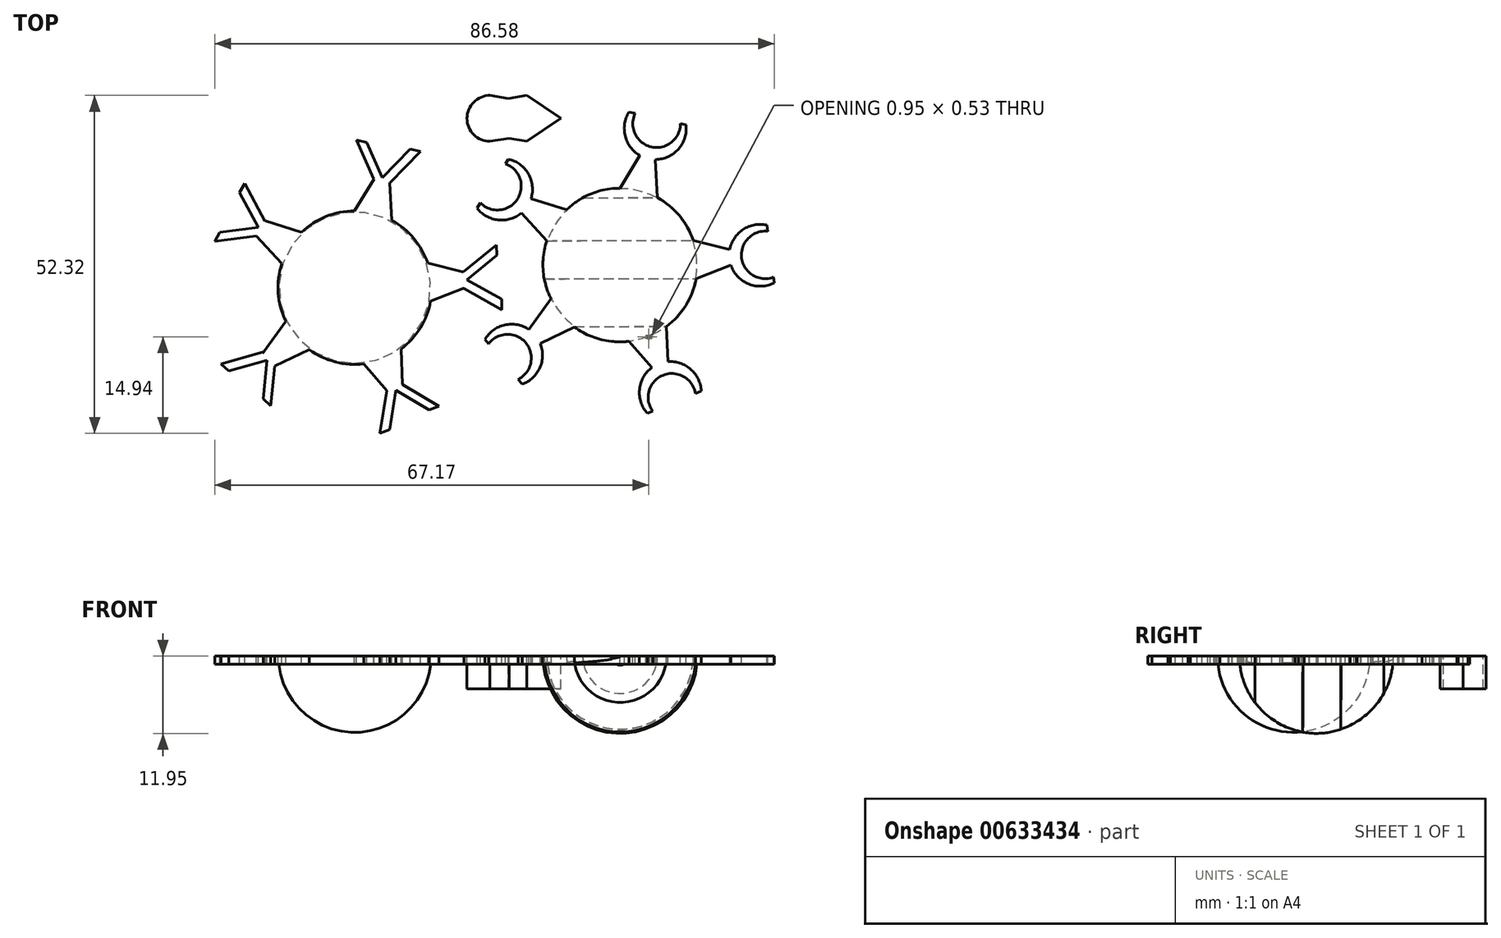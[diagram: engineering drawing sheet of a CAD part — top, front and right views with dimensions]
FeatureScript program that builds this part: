
annotation { "Feature Type Name" : "Feature", "Feature Type Description" : "" }
export const myFeature = defineFeature(function(context is Context, id is Id, definition is map)
    precondition{}
    {
        {
            var Q0;
            Q0=qCreatedBy(makeId("Top.planeOp"),FACE);
            var sketch = newSketch(context, id + "F0", { "sketchPlane" : qUnion([Q0])});
            skCircle(sketch, "E0.cCircle", {"center": v(0, 3.73) * mm, "radius": 12.26 * mm, "construction": true});
            skLineSegment(sketch, "E0.3", {"start": v(4.56, -7.66) * mm, "end": v(3.93, -7.5) * mm});
            skLineSegment(sketch, "E1", {"start": v(4.56, -7.66) * mm, "end": v(4.42, -7.3) * mm});
            skLineSegment(sketch, "E2", {"start": v(-14.6, 12.91) * mm, "end": v(-13.88, 14.05) * mm});
            skLineSegment(sketch, "E3", {"start": v(-13.88, 14.05) * mm, "end": v(-8.26, 12.28) * mm});
            skLineSegment(sketch, "E4", {"start": v(-14.6, 12.91) * mm, "end": v(-15.32, 11.77) * mm});
            skLineSegment(sketch, "E5", {"start": v(-15.32, 11.77) * mm, "end": v(-11.3, 7.45) * mm});
            skPoint(sketch, "E6.start.orphan", {"position": v(-10.38, 10.26) * mm});
            skLineSegment(sketch, "E7", {"start": v(-13.28, -7.35) * mm, "end": v(-14.16, -6.3) * mm});
            skLineSegment(sketch, "E8", {"start": v(-14.16, -6.3) * mm, "end": v(-10.69, -1.48) * mm});
            skLineSegment(sketch, "E9", {"start": v(-13.28, -7.35) * mm, "end": v(-12.38, -8.43) * mm});
            skLineSegment(sketch, "E10", {"start": v(-12.38, -8.43) * mm, "end": v(-7.05, -5.85) * mm});
            skLineSegment(sketch, "E11", {"start": v(6.18, -11.7) * mm, "end": v(4.96, -12.2) * mm});
            skLineSegment(sketch, "E12", {"start": v(4.96, -12.2) * mm, "end": v(1.38, -8.08) * mm});
            skLineSegment(sketch, "E13", {"start": v(6.18, -11.7) * mm, "end": v(7.36, -11.23) * mm});
            skLineSegment(sketch, "E14", {"start": v(7.36, -11.23) * mm, "end": v(7.16, -5.77) * mm});
            skLineSegment(sketch, "E15", {"start": v(17.02, 4.87) * mm, "end": v(17.1, 3.73) * mm});
            skLineSegment(sketch, "E16", {"start": v(17.1, 3.73) * mm, "end": v(11.7, 1.62) * mm});
            skLineSegment(sketch, "E17", {"start": v(17.02, 4.87) * mm, "end": v(16.94, 6.1) * mm});
            skLineSegment(sketch, "E18", {"start": v(16.94, 6.1) * mm, "end": v(11.26, 7.53) * mm});
            skLineSegment(sketch, "E19", {"start": v(5.42, 20.04) * mm, "end": v(5.72, 14.15) * mm});
            skLineSegment(sketch, "E20", {"start": v(3, 20.65) * mm, "end": v(-0.04, 15.62) * mm});
            skArc(sketch, "E21", {"start": v(-7.05, -5.85) * mm, "mid": v(-3.05, -7.76) * mm, "end": v(1.38, -8.08) * mm});
            skPoint(sketch, "E22.orphan", {"position": v(0, -6.5) * mm});
            skArc(sketch, "E23.trimOffspring", {"start": v(-11.3, 7.45) * mm, "mid": v(-11.86, 2.92) * mm, "end": v(-10.69, -1.48) * mm});
            skArc(sketch, "E24.trimOffspring", {"start": v(-0.04, 15.62) * mm, "mid": v(-4.47, 14.74) * mm, "end": v(-8.26, 12.28) * mm});
            skPoint(sketch, "E0.1.start.orphan", {"position": v(3, 15.62) * mm});
            skArc(sketch, "E25.trimOffspring", {"start": v(11.26, 7.53) * mm, "mid": v(9.12, 11.36) * mm, "end": v(5.72, 14.15) * mm});
            skLineSegment(sketch, "E26.trimOffspring", {"start": v(4.9, -7.1) * mm, "end": v(4.56, -7.66) * mm});
            skArc(sketch, "E27.trimOffspring", {"start": v(7.16, -5.77) * mm, "mid": v(10.13, -2.5) * mm, "end": v(11.7, 1.62) * mm});
            skArc(sketch, "E28", {"start": v(2.3, 27.2) * mm, "mid": v(4.82, 22) * mm, "end": v(9.3, 25.64) * mm});
            skArc(sketch, "E29", {"start": v(1.36, 27.41) * mm, "mid": v(0.75, 23.72) * mm, "end": v(2.98, 20.72) * mm});
            skLineSegment(sketch, "E30", {"start": v(1.36, 27.41) * mm, "end": v(2.3, 27.2) * mm});
            skLineSegment(sketch, "E31.trimOffspring", {"start": v(9.3, 25.64) * mm, "end": v(10.15, 25.45) * mm});
            skArc(sketch, "E32.trimOffspring", {"start": v(5.45, 20.06) * mm, "mid": v(9.01, 21.7) * mm, "end": v(10.15, 25.45) * mm});
            skLineSegment(sketch, "E33", {"start": v(3, 20.65) * mm, "end": v(2.98, 20.72) * mm});
            skPoint(sketch, "E34.orphan", {"position": v(4.2, 20.35) * mm});
            skLineSegment(sketch, "E35", {"start": v(5.42, 20.04) * mm, "end": v(5.45, 20.06) * mm});
            skArc(sketch, "E36", {"start": v(-21.63, 13.35) * mm, "mid": v(-15.9, 13.93) * mm, "end": v(-17.78, 19.38) * mm});
            skArc(sketch, "E37", {"start": v(-22.16, 12.53) * mm, "mid": v(-18.9, 10.7) * mm, "end": v(-15.32, 11.77) * mm});
            skLineSegment(sketch, "E38", {"start": v(-22.16, 12.53) * mm, "end": v(-21.63, 13.35) * mm});
            skLineSegment(sketch, "E39.trimOffspring", {"start": v(-17.78, 19.38) * mm, "end": v(-17.3, 20.12) * mm});
            skArc(sketch, "E40.trimOffspring", {"start": v(-13.85, 13.86) * mm, "mid": v(-14.17, 17.77) * mm, "end": v(-17.3, 20.12) * mm});
            skArc(sketch, "E41", {"start": v(22.8, 8.95) * mm, "mid": v(18.77, 4.81) * mm, "end": v(23.72, 1.84) * mm});
            skArc(sketch, "E42", {"start": v(22.67, 9.9) * mm, "mid": v(19, 9.22) * mm, "end": v(16.94, 6.1) * mm});
            skLineSegment(sketch, "E43", {"start": v(22.67, 9.9) * mm, "end": v(22.8, 8.95) * mm});
            skLineSegment(sketch, "E44.trimOffspring", {"start": v(23.72, 1.84) * mm, "end": v(23.83, 0.97) * mm});
            skArc(sketch, "E45.trimOffspring", {"start": v(17.16, 3.55) * mm, "mid": v(19.92, 0.77) * mm, "end": v(23.83, 0.97) * mm});
            skLineSegment(sketch, "E46", {"start": v(17.16, 3.55) * mm, "end": v(17.1, 3.73) * mm});
            skArc(sketch, "E47", {"start": v(-15.8, -13.97) * mm, "mid": v(-14.62, -8.33) * mm, "end": v(-20.38, -8.47) * mm});
            skArc(sketch, "E48", {"start": v(-15.17, -14.72) * mm, "mid": v(-12.44, -12.17) * mm, "end": v(-12.38, -8.43) * mm});
            skLineSegment(sketch, "E49", {"start": v(-15.17, -14.72) * mm, "end": v(-15.8, -13.97) * mm});
            skLineSegment(sketch, "E50.trimOffspring", {"start": v(-20.38, -8.47) * mm, "end": v(-20.94, -7.8) * mm});
            skArc(sketch, "E51.trimOffspring", {"start": v(-13.93, -6.4) * mm, "mid": v(-17.75, -5.53) * mm, "end": v(-20.94, -7.8) * mm});
            skArc(sketch, "E52", {"start": v(11.62, -16.16) * mm, "mid": v(6.59, -13.34) * mm, "end": v(5, -18.89) * mm});
            skArc(sketch, "E53", {"start": v(12.52, -15.79) * mm, "mid": v(10.9, -12.42) * mm, "end": v(7.36, -11.23) * mm});
            skLineSegment(sketch, "E54", {"start": v(12.52, -15.79) * mm, "end": v(11.62, -16.16) * mm});
            skLineSegment(sketch, "E55.trimOffspring", {"start": v(5, -18.89) * mm, "end": v(4.19, -19.22) * mm});
            skArc(sketch, "E56.trimOffspring", {"start": v(4.95, -12.11) * mm, "mid": v(2.98, -15.5) * mm, "end": v(4.19, -19.22) * mm});
            skArc(sketch, "E57", {"start": v(0, -8.16) * mm, "mid": v(11.92, 3.75) * mm, "end": v(-0.04, 15.62) * mm});
            skLineSegment(sketch, "E58", {"start": v(0, -8.16) * mm, "end": v(-0.04, 15.62) * mm});
            skSolve(sketch);
        }
        {
            var Q0;
            Q0=qCreatedBy(makeId("Top.planeOp"),FACE);
            var sketch = newSketch(context, id + "F1", { "sketchPlane" : qUnion([Q0])});
            skCircle(sketch, "E59.cCircle", {"center": v(-41.06, 0.22) * mm, "radius": 12.26 * mm, "construction": true});
            skLineSegment(sketch, "E60", {"start": v(-55.66, 9.4) * mm, "end": v(-54.94, 10.54) * mm});
            skLineSegment(sketch, "E61", {"start": v(-54.94, 10.54) * mm, "end": v(-49.32, 8.78) * mm});
            skLineSegment(sketch, "E62", {"start": v(-55.66, 9.4) * mm, "end": v(-56.38, 8.26) * mm});
            skLineSegment(sketch, "E63", {"start": v(-56.38, 8.26) * mm, "end": v(-52.35, 3.94) * mm});
            skPoint(sketch, "E64.start.orphan", {"position": v(-51.44, 6.75) * mm});
            skLineSegment(sketch, "E65", {"start": v(-54.34, -10.85) * mm, "end": v(-55.22, -9.8) * mm});
            skLineSegment(sketch, "E66", {"start": v(-55.22, -9.8) * mm, "end": v(-51.75, -4.98) * mm});
            skLineSegment(sketch, "E67", {"start": v(-54.34, -10.85) * mm, "end": v(-53.44, -11.94) * mm});
            skLineSegment(sketch, "E68", {"start": v(-53.44, -11.94) * mm, "end": v(-48.11, -9.35) * mm});
            skLineSegment(sketch, "E69", {"start": v(-34.88, -15.21) * mm, "end": v(-36.1, -15.7) * mm});
            skLineSegment(sketch, "E70", {"start": v(-36.1, -15.7) * mm, "end": v(-39.68, -11.59) * mm});
            skLineSegment(sketch, "E71", {"start": v(-34.88, -15.21) * mm, "end": v(-33.7, -14.74) * mm});
            skLineSegment(sketch, "E72", {"start": v(-33.7, -14.74) * mm, "end": v(-33.9, -9.27) * mm});
            skLineSegment(sketch, "E73", {"start": v(-24.04, 1.36) * mm, "end": v(-23.96, 0.22) * mm});
            skLineSegment(sketch, "E74", {"start": v(-23.96, 0.22) * mm, "end": v(-29.36, -1.88) * mm});
            skLineSegment(sketch, "E75", {"start": v(-24.04, 1.36) * mm, "end": v(-24.12, 2.6) * mm});
            skLineSegment(sketch, "E76", {"start": v(-24.12, 2.6) * mm, "end": v(-29.8, 4.03) * mm});
            skLineSegment(sketch, "E77", {"start": v(-36.86, 16.85) * mm, "end": v(-35.64, 16.54) * mm});
            skLineSegment(sketch, "E78", {"start": v(-35.64, 16.54) * mm, "end": v(-35.34, 10.64) * mm});
            skLineSegment(sketch, "E79", {"start": v(-36.86, 16.85) * mm, "end": v(-38.06, 17.15) * mm});
            skLineSegment(sketch, "E80", {"start": v(-38.06, 17.15) * mm, "end": v(-41.1, 12.11) * mm});
            skArc(sketch, "E81", {"start": v(-29.8, 4.03) * mm, "mid": v(-31.94, 7.86) * mm, "end": v(-35.34, 10.64) * mm});
            skArc(sketch, "E82.trimOffspring", {"start": v(-33.9, -9.27) * mm, "mid": v(-30.93, -6) * mm, "end": v(-29.36, -1.88) * mm});
            skArc(sketch, "E83.trimOffspring", {"start": v(-48.11, -9.35) * mm, "mid": v(-44.11, -11.27) * mm, "end": v(-39.68, -11.59) * mm});
            skArc(sketch, "E84.trimOffspring", {"start": v(-52.35, 3.94) * mm, "mid": v(-52.92, -0.58) * mm, "end": v(-51.75, -4.98) * mm});
            skArc(sketch, "E85.trimOffspring", {"start": v(-41.1, 12.11) * mm, "mid": v(-45.53, 11.24) * mm, "end": v(-49.32, 8.78) * mm});
            skPoint(sketch, "E86.start.orphan", {"position": v(-38.06, 12.11) * mm});
            skLineSegment(sketch, "E87", {"start": v(-35.67, -21.72) * mm, "end": v(-34.7, -15.64) * mm});
            skLineSegment(sketch, "E88", {"start": v(-34.7, -15.64) * mm, "end": v(-29.55, -18.7) * mm});
            skLineSegment(sketch, "E89", {"start": v(-36.1, -15.7) * mm, "end": v(-37.19, -22.33) * mm});
            skLineSegment(sketch, "E90", {"start": v(-37.19, -22.33) * mm, "end": v(-35.67, -21.72) * mm});
            skLineSegment(sketch, "E91", {"start": v(-33.7, -14.74) * mm, "end": v(-28.06, -18.1) * mm});
            skLineSegment(sketch, "E92", {"start": v(-28.06, -18.1) * mm, "end": v(-29.55, -18.7) * mm});
            skLineSegment(sketch, "E93", {"start": v(-54.32, -10.67) * mm, "end": v(-55.28, -9.77) * mm});
            skLineSegment(sketch, "E94", {"start": v(-54.32, -10.67) * mm, "end": v(-53.4, -11.54) * mm});
            skLineSegment(sketch, "E95", {"start": v(-60.56, -12.7) * mm, "end": v(-54.63, -11.02) * mm});
            skLineSegment(sketch, "E96", {"start": v(-54.63, -11.02) * mm, "end": v(-55.24, -16.97) * mm});
            skLineSegment(sketch, "E97", {"start": v(-55.28, -9.77) * mm, "end": v(-61.74, -11.58) * mm});
            skLineSegment(sketch, "E98", {"start": v(-61.74, -11.58) * mm, "end": v(-60.56, -12.7) * mm});
            skLineSegment(sketch, "E99", {"start": v(-53.4, -11.54) * mm, "end": v(-54.06, -18.08) * mm});
            skLineSegment(sketch, "E100", {"start": v(-54.06, -18.08) * mm, "end": v(-55.24, -16.97) * mm});
            skLineSegment(sketch, "E101", {"start": v(-24.2, 1.4) * mm, "end": v(-24.17, 0.1) * mm});
            skLineSegment(sketch, "E102", {"start": v(-24.2, 1.4) * mm, "end": v(-24.25, 2.68) * mm});
            skLineSegment(sketch, "E103", {"start": v(-18.36, -1.56) * mm, "end": v(-23.74, 1.43) * mm});
            skLineSegment(sketch, "E104", {"start": v(-23.74, 1.43) * mm, "end": v(-19.1, 5.21) * mm});
            skLineSegment(sketch, "E105", {"start": v(-24.17, 0.1) * mm, "end": v(-18.31, -3.2) * mm});
            skLineSegment(sketch, "E106", {"start": v(-18.31, -3.2) * mm, "end": v(-18.36, -1.56) * mm});
            skLineSegment(sketch, "E107", {"start": v(-24.25, 2.68) * mm, "end": v(-19.15, 6.83) * mm});
            skLineSegment(sketch, "E108", {"start": v(-19.15, 6.83) * mm, "end": v(-19.1, 5.21) * mm});
            skLineSegment(sketch, "E109", {"start": v(-36.9, 16.79) * mm, "end": v(-35.61, 16.49) * mm});
            skLineSegment(sketch, "E110", {"start": v(-36.9, 16.79) * mm, "end": v(-38.13, 17.08) * mm});
            skLineSegment(sketch, "E111", {"start": v(-32.51, 21.66) * mm, "end": v(-36.8, 17.25) * mm});
            skLineSegment(sketch, "E112", {"start": v(-36.8, 17.25) * mm, "end": v(-39.25, 22.7) * mm});
            skLineSegment(sketch, "E113", {"start": v(-35.61, 16.49) * mm, "end": v(-30.92, 21.3) * mm});
            skLineSegment(sketch, "E114", {"start": v(-30.92, 21.3) * mm, "end": v(-32.51, 21.66) * mm});
            skLineSegment(sketch, "E115", {"start": v(-38.13, 17.08) * mm, "end": v(-40.82, 23.07) * mm});
            skLineSegment(sketch, "E116", {"start": v(-40.82, 23.07) * mm, "end": v(-39.25, 22.7) * mm});
            skLineSegment(sketch, "E117", {"start": v(-55.58, 9.32) * mm, "end": v(-54.92, 10.45) * mm});
            skLineSegment(sketch, "E118", {"start": v(-55.58, 9.32) * mm, "end": v(-56.22, 8.22) * mm});
            skLineSegment(sketch, "E119", {"start": v(-58.94, 14.95) * mm, "end": v(-56, 9.54) * mm});
            skLineSegment(sketch, "E120", {"start": v(-56, 9.54) * mm, "end": v(-61.93, 8.82) * mm});
            skLineSegment(sketch, "E121", {"start": v(-54.92, 10.45) * mm, "end": v(-58.12, 16.35) * mm});
            skLineSegment(sketch, "E122", {"start": v(-58.12, 16.35) * mm, "end": v(-58.94, 14.95) * mm});
            skLineSegment(sketch, "E123", {"start": v(-56.22, 8.22) * mm, "end": v(-62.75, 7.43) * mm});
            skLineSegment(sketch, "E124", {"start": v(-62.75, 7.43) * mm, "end": v(-61.93, 8.82) * mm});
            skCircle(sketch, "E125", {"center": v(-41.06, 0.22) * mm, "radius": 11.78 * mm});
            skLineSegment(sketch, "E126", {"start": v(-41.1, 12.11) * mm, "end": v(-41.1, 12) * mm});
            skPoint(sketch, "E127.start.orphan", {"position": v(-41.06, -11.55) * mm});
            skLineSegment(sketch, "E128", {"start": v(-41.1, 12) * mm, "end": v(-41.06, -11.55) * mm});
            skSolve(sketch);
        }
        {
            var Q0;
            Q0=qCreatedBy(makeId("Top.planeOp"),FACE);
            var sketch = newSketch(context, id + "F2", { "sketchPlane" : qUnion([Q0])});
            skArc(sketch, "E129", {"start": v(-20.15, 30) * mm, "mid": v(-23.72, 26.43) * mm, "end": v(-20.15, 22.86) * mm});
            skLineSegment(sketch, "E130", {"start": v(-14.46, 30) * mm, "end": v(-9.2, 26.43) * mm});
            skLineSegment(sketch, "E131", {"start": v(-9.2, 26.43) * mm, "end": v(-14.46, 22.86) * mm});
            skLineSegment(sketch, "E132", {"start": v(-20.15, 30) * mm, "end": v(-17.3, 29.5) * mm});
            skLineSegment(sketch, "E133", {"start": v(-17.3, 29.5) * mm, "end": v(-14.46, 30) * mm});
            skLineSegment(sketch, "E134", {"start": v(-20.15, 22.86) * mm, "end": v(-17.22, 23.37) * mm});
            skLineSegment(sketch, "E135", {"start": v(-17.22, 23.37) * mm, "end": v(-14.46, 22.86) * mm});
            skPoint(sketch, "E136.end.orphan", {"position": v(-20.15, 29.5) * mm});
            skPoint(sketch, "E137.start.orphan", {"position": v(-14.46, 29.5) * mm});
            skPoint(sketch, "E138.start.orphan", {"position": v(-20.15, 23.37) * mm});
            skLineSegment(sketch, "E139", {"start": v(-20.15, 30) * mm, "end": v(-20.15, 22.86) * mm});
            skLineSegment(sketch, "E140", {"start": v(-14.46, 30) * mm, "end": v(-14.46, 22.86) * mm});
            skSolve(sketch);
        }
        {
            var Q0;
            Q0 = qSketchRegion(id + "F0", true);
            var Q1;
            Q1 = qSketchRegion(id + "F1", true);
            var Q2;
            Q2=makeQuery(id+"F1.imprint","IMPRINT",FACE,{"disambiguationData":[TD([[makeQuery(id+"F1.imprint","IMPRINT",EDGE,{"derivedFrom":sQuery(id+"F1.wireOp",EDGE,"lYwTOjgy-X5ZI-BHur-sRZn-WGW1JGmxqnTo")}),1.0]])]});
            var Q3;
            Q3=makeQuery(id+"F1.imprint","IMPRINT",FACE,{"disambiguationData":[TD([[makeQuery(id+"F1.imprint","IMPRINT",EDGE,{"derivedFrom":sQuery(id+"F1.wireOp",EDGE,"gC46bDGC-LVJ8-fxy5-nFBz-ZXnn0VK3JdZ0")}),1.0]])]});
            var Q4;
            Q4=makeQuery(id+"F1.imprint","IMPRINT",FACE,{"disambiguationData":[TD([[makeQuery(id+"F1.imprint","IMPRINT",EDGE,{"derivedFrom":sQuery(id+"F1.wireOp",EDGE,"E125")}),1.0]])]});
            extrude(context, id + "F3", {"entities" : qUnion([Q0, Q1, Q2, Q3, Q4]), "oppositeDirection" : true, "depth" : 1.27 * mm, "offsetDistance" : 25.4 * mm});
        }
        {
            var Q0;
            {var subQ0=sQuery(id+"F1.wireOp",EDGE,"E128");Q0=makeQuery(id+"F1.imprint","IMPRINT",FACE,{"disambiguationData":[TD([[makeQuery(id+"F1.imprint","IMPRINT",EDGE,{"derivedFrom":subQ0}),1.0]])]});}
            var Q1;
            Q1=sQuery(id+"F1.wireOp",EDGE,"E128");
            revolve(context, id + "F4", {"operationType" : NewBodyOperationType.ADD, "entities" : qUnion([Q0]), "axis" : qUnion([Q1]), "revolveType" : RevolveType.ONE_DIRECTION, "oppositeDirection" : true, "angle" : 180 * degree});
        }
        {
            var Q0;
            {var subQ7=sQuery(id+"F0.wireOp",EDGE,"E25.trimOffspring");Q0=makeQuery(id+"F0.imprint","IMPRINT",FACE,{"disambiguationData":[TD([[makeQuery(id+"F0.imprint","IMPRINT",EDGE,{"derivedFrom":subQ7}),1.0]])]});}
            var Q1;
            Q1=sQuery(id+"F0.wireOp",EDGE,"E58");
            revolve(context, id + "F5", {"operationType" : NewBodyOperationType.ADD, "entities" : qUnion([Q0]), "axis" : qUnion([Q1]), "revolveType" : RevolveType.ONE_DIRECTION, "angle" : 180 * degree});
        }
        {
            var Q0;
            Q0=makeQuery(id+"F2.imprint","IMPRINT",FACE,{"disambiguationData":[TD([[makeQuery(id+"F2.imprint","IMPRINT",EDGE,{"derivedFrom":sQuery(id+"F2.wireOp",EDGE,"E132")}),-1.0]])]});
            var Q1;
            Q1=makeQuery(id+"F2.imprint","IMPRINT",FACE,{"disambiguationData":[TD([[makeQuery(id+"F2.imprint","IMPRINT",EDGE,{"derivedFrom":sQuery(id+"F2.wireOp",EDGE,"E130")}),-1.0]])]});
            var Q2;
            Q2=makeQuery(id+"F2.imprint","IMPRINT",FACE,{"disambiguationData":[TD([[makeQuery(id+"F2.imprint","IMPRINT",EDGE,{"derivedFrom":sQuery(id+"F2.wireOp",EDGE,"E129")}),1.0]])]});
            extrude(context, id + "F6", {"entities" : qUnion([Q0, Q1, Q2]), "oppositeDirection" : true, "depth" : 5.08 * mm, "offsetDistance" : 25.4 * mm});
        }
    });
